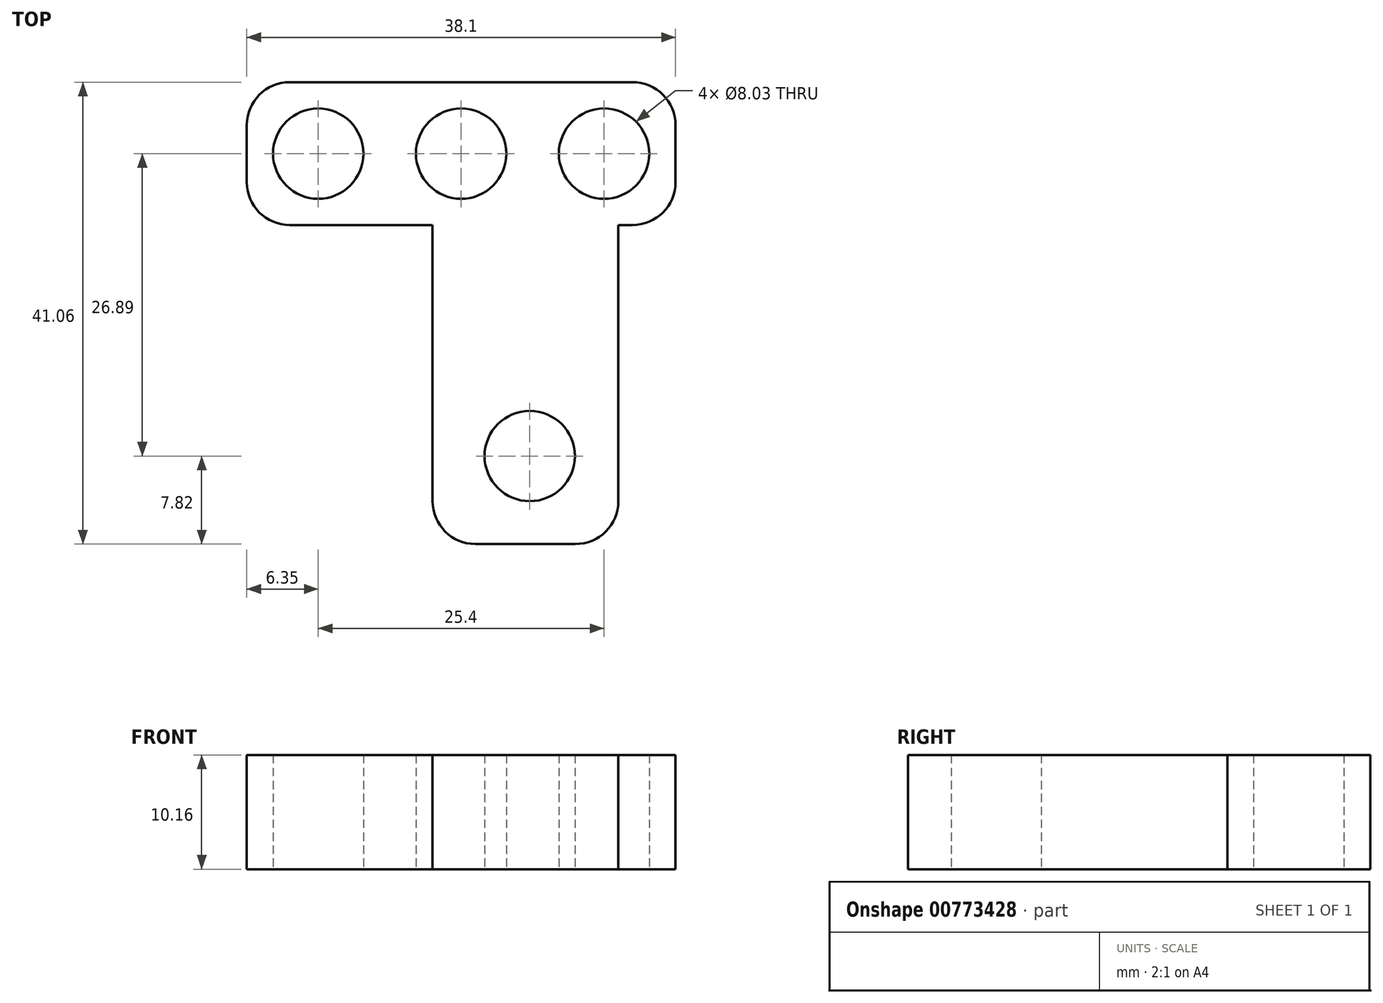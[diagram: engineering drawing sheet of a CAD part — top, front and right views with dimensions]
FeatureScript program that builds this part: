
annotation { "Feature Type Name" : "Feature", "Feature Type Description" : "" }
export const myFeature = defineFeature(function(context is Context, id is Id, definition is map)
    precondition{}
    {
        {
            var Q0;
            Q0=qCreatedBy(makeId("Top.planeOp"),FACE);
            var sketch = newSketch(context, id + "F0", { "sketchPlane" : qUnion([Q0])});
            skLineSegment(sketch, "E0.bottom", {"start": v(19.05, -6.35) * mm, "end": v(-19.05, -6.35) * mm});
            skLineSegment(sketch, "E0.top", {"start": v(19.05, 6.35) * mm, "end": v(-19.05, 6.35) * mm});
            skLineSegment(sketch, "E0.left", {"start": v(19.05, -6.35) * mm, "end": v(19.05, 6.35) * mm});
            skLineSegment(sketch, "E0.right", {"start": v(-19.05, -6.35) * mm, "end": v(-19.05, 6.35) * mm});
            skPoint(sketch, "E0.middle", {"position": v(0, 0) * mm});
            skLineSegment(sketch, "E1.bottom", {"start": v(-2.54, -6.35) * mm, "end": v(13.97, -6.35) * mm});
            skLineSegment(sketch, "E1.top", {"start": v(-2.54, -34.71) * mm, "end": v(13.97, -34.71) * mm});
            skLineSegment(sketch, "E1.left", {"start": v(-2.54, -6.35) * mm, "end": v(-2.54, -34.71) * mm});
            skLineSegment(sketch, "E1.right", {"start": v(13.97, -6.35) * mm, "end": v(13.97, -34.71) * mm});
            skCircle(sketch, "E2", {"center": v(0, 0) * mm, "radius": 4.01 * mm});
            skCircle(sketch, "E3", {"center": v(-12.7, 0) * mm, "radius": 4.01 * mm});
            skCircle(sketch, "E4", {"center": v(12.7, 0) * mm, "radius": 4.01 * mm});
            skPoint(sketch, "E5.centerSnap0", {"position": v(5.71, -34.71) * mm});
            skCircle(sketch, "E6", {"center": v(6.1, -26.89) * mm, "radius": 4.01 * mm});
            skSolve(sketch);
        }
        {
            var Q0;
            Q0=makeQuery(id+"F0.imprint","IMPRINT",FACE,{"disambiguationData":[TD([[makeQuery(id+"F0.imprint","IMPRINT",EDGE,{"derivedFrom":sQuery(id+"F0.wireOp",EDGE,"E0.top")}),1.0]])]});
            var Q1;
            Q1=makeQuery(id+"F0.imprint","IMPRINT",FACE,{"disambiguationData":[TD([[makeQuery(id+"F0.imprint","IMPRINT",EDGE,{"derivedFrom":sQuery(id+"F0.wireOp",EDGE,"E1.top")}),1.0]])]});
            extrude(context, id + "F1", {"entities" : qUnion([Q0, Q1]), "depth" : 10.16 * mm});
        }
        {
            var Q0;
            Q0=makeQuery(id+"F1.opExtrude","SWEPT_EDGE",EDGE,{"disambiguationData":[OSD([sQuery(id+"F0.wireOp",EDGE,"E1.top"),sQuery(id+"F0.wireOp",EDGE,"E1.left")])]});
            var Q1;
            Q1=makeQuery(id+"F1.opExtrude","SWEPT_EDGE",EDGE,{"disambiguationData":[OSD([sQuery(id+"F0.wireOp",EDGE,"E1.top"),sQuery(id+"F0.wireOp",EDGE,"E1.right")])]});
            var Q2;
            Q2=makeQuery(id+"F1.opExtrude","SWEPT_EDGE",EDGE,{"disambiguationData":[OSD([sQuery(id+"F0.wireOp",EDGE,"E0.bottom"),sQuery(id+"F0.wireOp",EDGE,"E0.left")])]});
            var Q3;
            Q3=makeQuery(id+"F1.opExtrude","SWEPT_EDGE",EDGE,{"disambiguationData":[OSD([sQuery(id+"F0.wireOp",EDGE,"E0.top"),sQuery(id+"F0.wireOp",EDGE,"E0.left")])]});
            var Q4;
            Q4=makeQuery(id+"F1.opExtrude","SWEPT_EDGE",EDGE,{"disambiguationData":[OSD([sQuery(id+"F0.wireOp",EDGE,"E0.bottom"),sQuery(id+"F0.wireOp",EDGE,"E0.right")])]});
            var Q5;
            Q5=makeQuery(id+"F1.opExtrude","SWEPT_EDGE",EDGE,{"disambiguationData":[OSD([sQuery(id+"F0.wireOp",EDGE,"E0.top"),sQuery(id+"F0.wireOp",EDGE,"E0.right")])]});
            fillet(context, id + "F2", {"entities" : qUnion([Q0, Q1, Q2, Q3, Q4, Q5]), "radius" : 3.8 * mm, "tangentPropagation" : true, "allowEdgeOverflow" : false});
        }
    });
